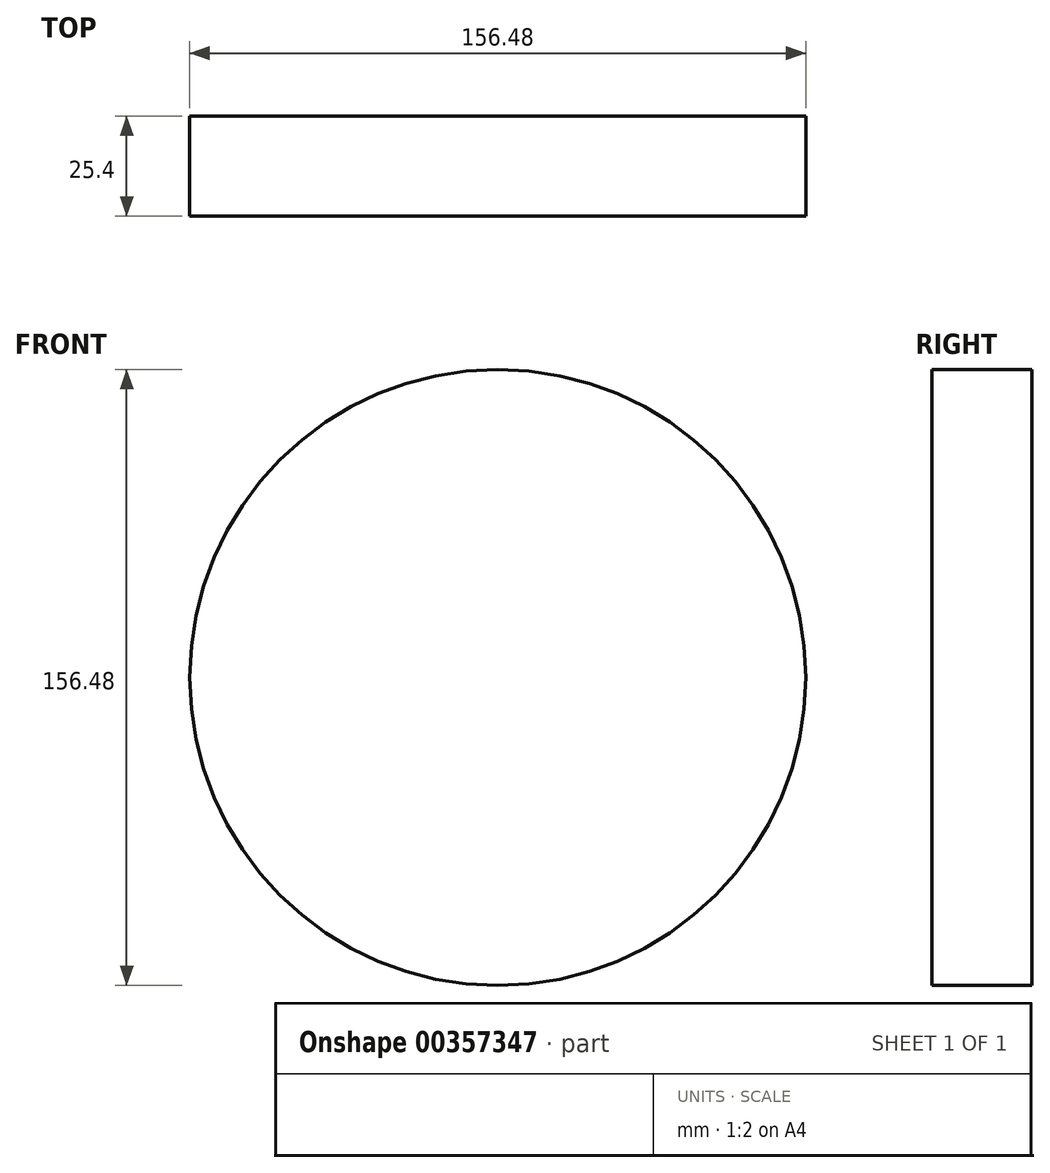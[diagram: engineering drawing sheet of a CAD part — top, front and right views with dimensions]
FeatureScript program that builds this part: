
annotation { "Feature Type Name" : "Feature", "Feature Type Description" : "" }
export const myFeature = defineFeature(function(context is Context, id is Id, definition is map)
    precondition{}
    {
        {
            var Q0;
            Q0=qCreatedBy(makeId("Front.planeOp"),FACE);
            var sketch = newSketch(context, id + "F0", { "sketchPlane" : qUnion([Q0])});
            skCircle(sketch, "E0", {"center": v(0, 0) * mm, "radius": 78.24 * mm});
            skSolve(sketch);
        }
        {
            var Q0;
            Q0=makeQuery(id+"F0.imprint","IMPRINT",FACE,{"disambiguationData":[TD([[makeQuery(id+"F0.imprint","IMPRINT",EDGE,{"derivedFrom":sQuery(id+"F0.wireOp",EDGE,"E0")}),1.0]])]});
            extrude(context, id + "F1", {"entities" : qUnion([Q0]), "depth" : 25.4 * mm});
        }
    });
